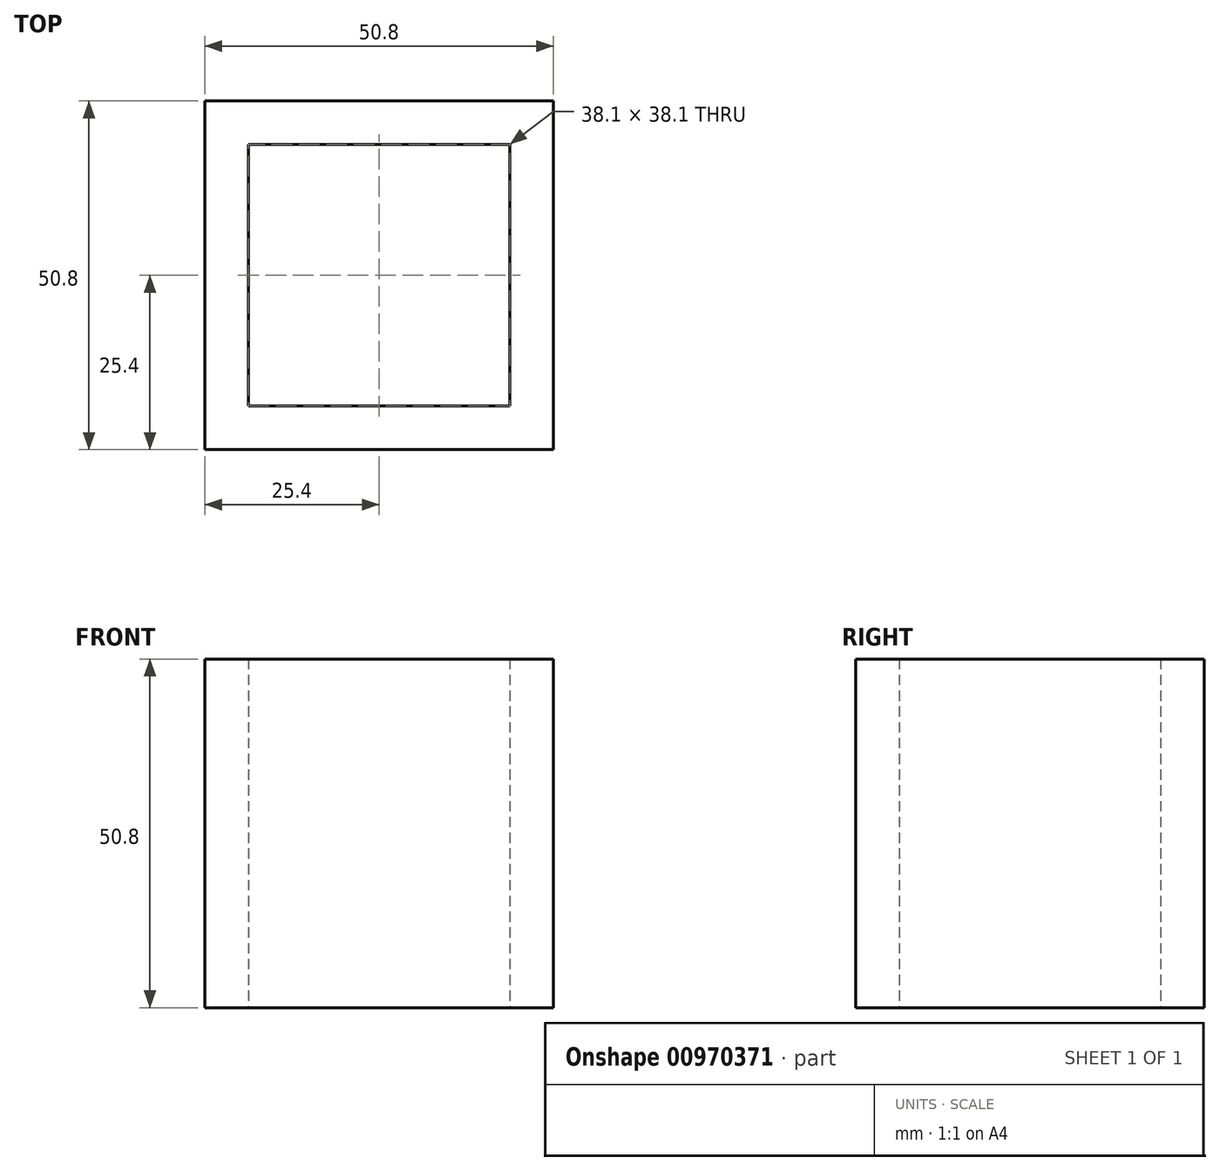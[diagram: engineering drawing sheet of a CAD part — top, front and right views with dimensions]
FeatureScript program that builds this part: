
annotation { "Feature Type Name" : "Feature", "Feature Type Description" : "" }
export const myFeature = defineFeature(function(context is Context, id is Id, definition is map)
    precondition{}
    {
        {
            var Q0;
            Q0=qCreatedBy(makeId("Top.planeOp"),FACE);
            var sketch = newSketch(context, id + "F0", { "sketchPlane" : qUnion([Q0])});
            skLineSegment(sketch, "E0.bottom", {"start": v(0, 0) * mm, "end": v(50.8, 0) * mm});
            skLineSegment(sketch, "E0.top", {"start": v(0, -50.8) * mm, "end": v(50.8, -50.8) * mm});
            skLineSegment(sketch, "E0.left", {"start": v(0, 0) * mm, "end": v(0, -50.8) * mm});
            skLineSegment(sketch, "E0.right", {"start": v(50.8, 0) * mm, "end": v(50.8, -50.8) * mm});
            skLineSegment(sketch, "E1.bottom", {"start": v(6.35, -6.35) * mm, "end": v(44.45, -6.35) * mm});
            skLineSegment(sketch, "E1.top", {"start": v(6.35, -44.45) * mm, "end": v(44.45, -44.45) * mm});
            skLineSegment(sketch, "E1.left", {"start": v(6.35, -6.35) * mm, "end": v(6.35, -44.45) * mm});
            skLineSegment(sketch, "E1.right", {"start": v(44.45, -6.35) * mm, "end": v(44.45, -44.45) * mm});
            skSolve(sketch);
        }
        {
            var Q0;
            Q0=makeQuery(id+"F0.imprint","IMPRINT",FACE,{"disambiguationData":[TD([[makeQuery(id+"F0.imprint","IMPRINT",EDGE,{"derivedFrom":sQuery(id+"F0.wireOp",EDGE,"E0.bottom")}),-1.0]])]});
            extrude(context, id + "F1", {"entities" : qUnion([Q0]), "depth" : 50.8 * mm, "offsetDistance" : 25.4 * mm});
        }
    });
